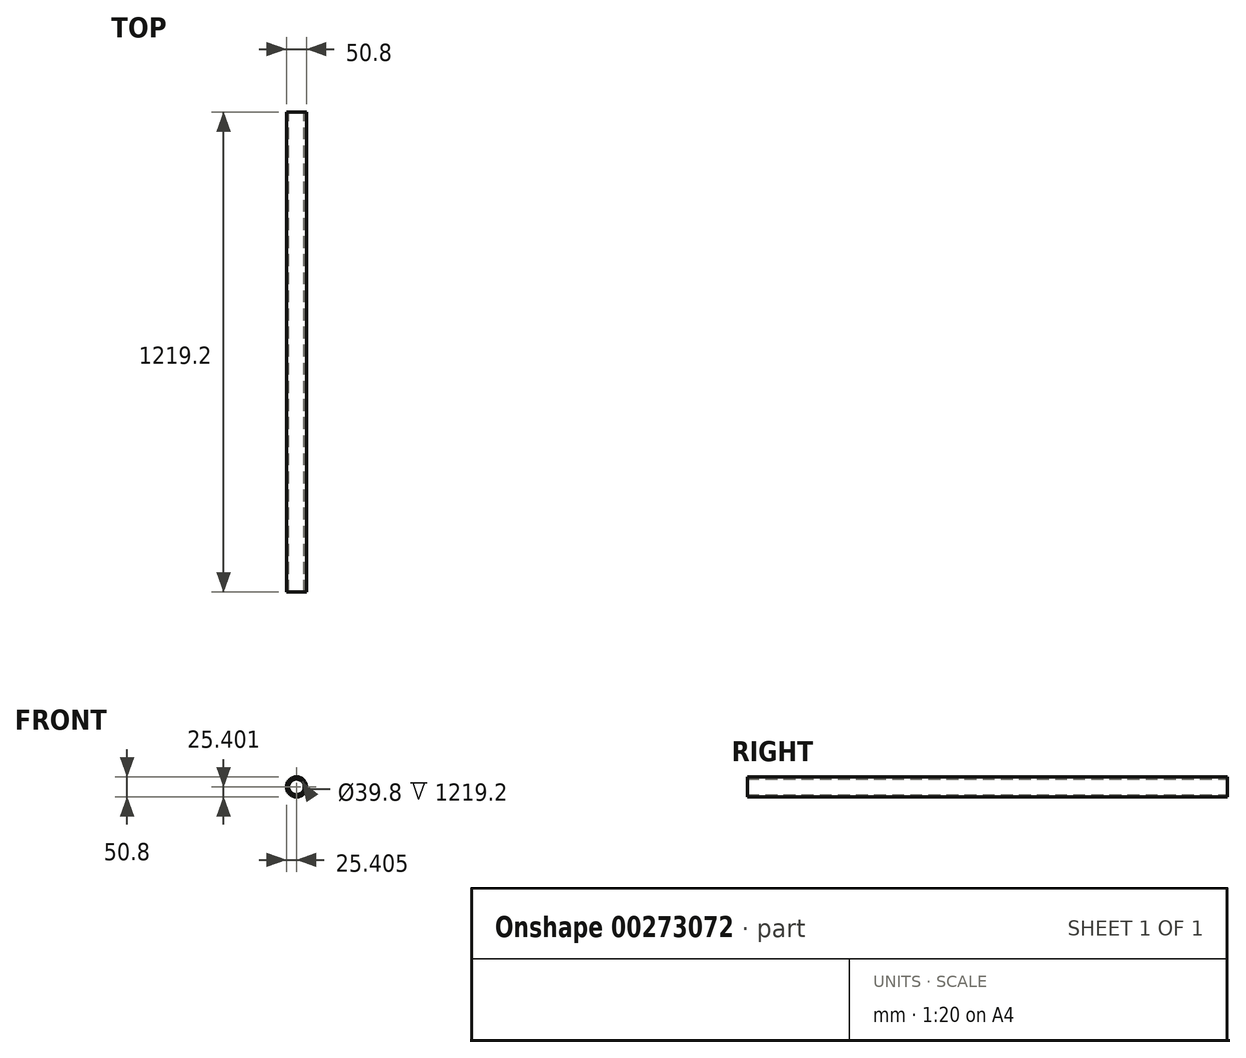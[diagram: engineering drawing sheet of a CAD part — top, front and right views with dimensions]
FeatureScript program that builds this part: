
annotation { "Feature Type Name" : "Feature", "Feature Type Description" : "" }
export const myFeature = defineFeature(function(context is Context, id is Id, definition is map)
    precondition{}
    {
        {
            var Q0;
            Q0=qCreatedBy(makeId("Front.planeOp"),FACE);
            var sketch = newSketch(context, id + "F0", { "sketchPlane" : qUnion([Q0])});
            skCircle(sketch, "E0", {"center": v(-8.78, 55.5) * mm, "radius": 25.4 * mm});
            skCircle(sketch, "E1", {"center": v(-8.78, 55.5) * mm, "radius": 19.9 * mm});
            skSolve(sketch);
        }
        {
            var Q0;
            Q0 = qSketchRegion(id + "F0", true);
            extrude(context, id + "F1", {"entities" : qUnion([Q0]), "depth" : 1219.2 * mm});
        }
    });
